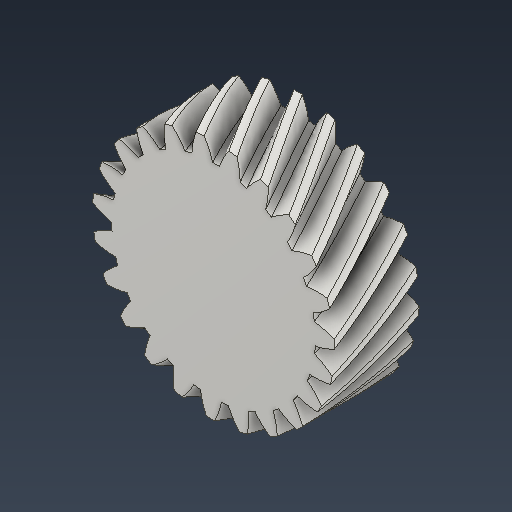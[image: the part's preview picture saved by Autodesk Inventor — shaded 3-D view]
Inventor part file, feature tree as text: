
AUTODESK INVENTOR PART (.ipt)
format: ipt  version: 2022 (Build 260153000, 153)  size: 560,128 bytes
history: native  units: mm (DEFAULTED — no unit token found)
features: plane x3, other x3, sketch x2, extrude x1
ambient origin geometry x8: Origin, YZ Plane, XZ Plane, XY Plane, X Axis, Y Axis, Z Axis, Center Point
bodies: Solid1 (feature_tree)
feature tree (9):
  extrude  "Extrusion1"  Depth=20.0mm TaperAngle=0.0deg
  plane  "Work Plane2"
  plane  "Work Plane8"
  plane  "Work Plane9"
  other  "Spur Gear"
  sketch  "Sketch1"  dims[d0=57.116225mm d1=20.0mm d2=0.0mm]
  sketch  "Sketch2"  dims[d3=53.116225mm d4=10.0mm d5=0.0mm d16=39.259818mm d17=0.0mm d34=1.36591mm d39=0.0mm d41=0.0mm d43=39.259818mm d46=39.259818mm d47=0.0mm d48=0.0mm]
  other  "Srf1"
  other  "Pitch Diameter"
